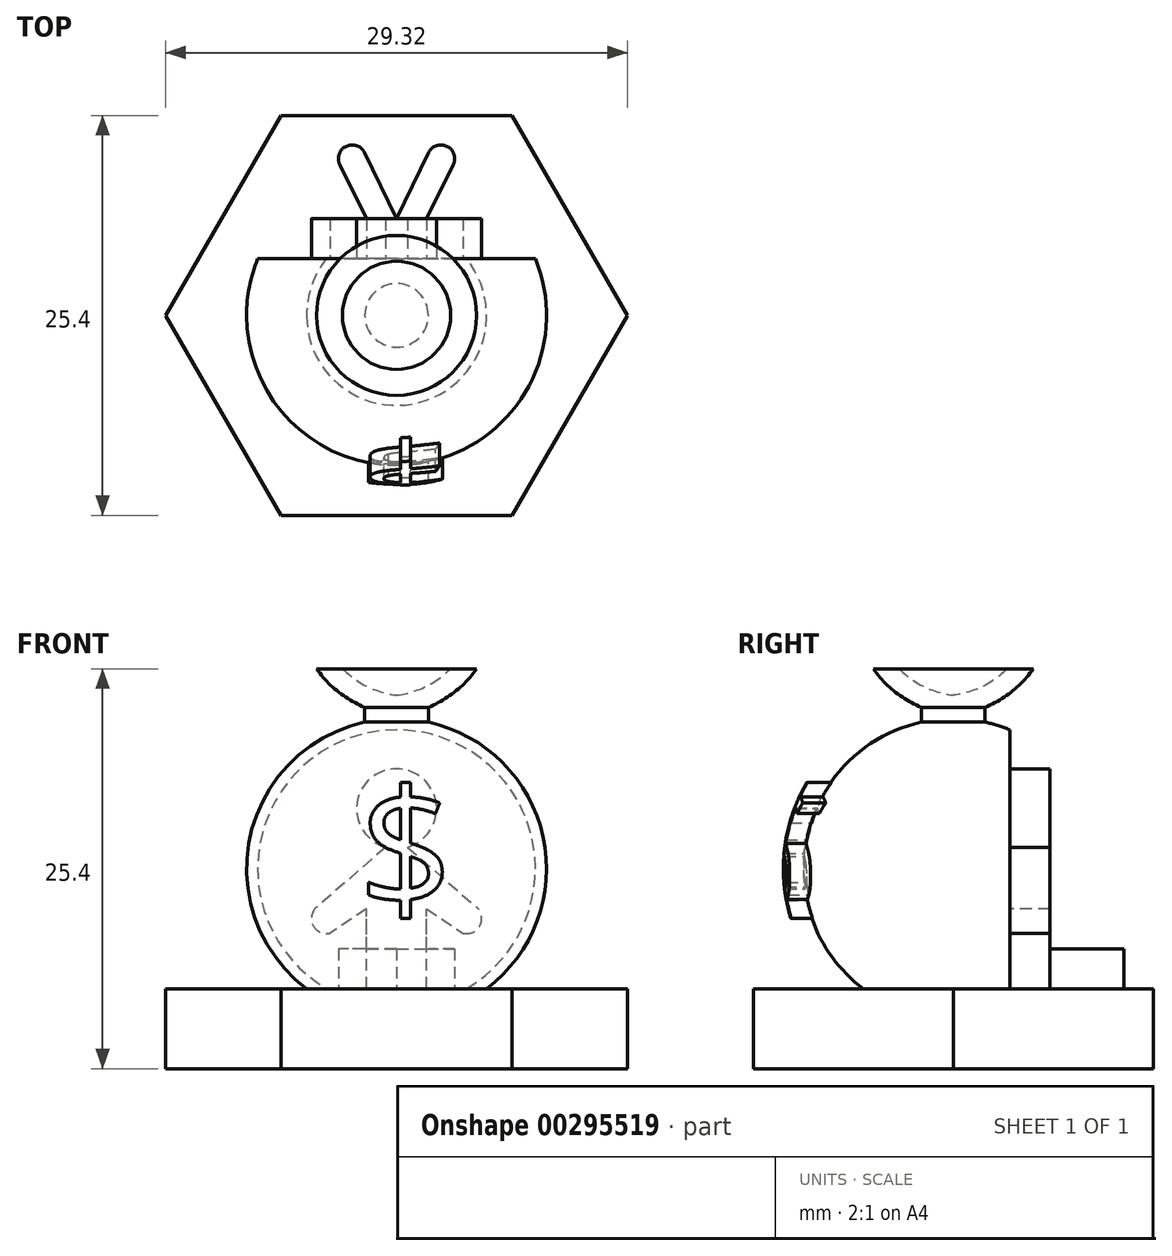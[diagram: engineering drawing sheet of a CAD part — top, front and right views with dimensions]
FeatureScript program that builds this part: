
annotation { "Feature Type Name" : "Feature", "Feature Type Description" : "" }
export const myFeature = defineFeature(function(context is Context, id is Id, definition is map)
    precondition{}
    {
        {
            var Q0;
            Q0=qCreatedBy(makeId("Top.planeOp"),FACE);
            var sketch = newSketch(context, id + "F0", { "sketchPlane" : qUnion([Q0])});
            skCircle(sketch, "E0.cCircle", {"center": v(0, 0) * mm, "radius": 12.7 * mm, "construction": true});
            skLineSegment(sketch, "E0.0", {"start": v(7.33, 12.7) * mm, "end": v(14.66, 0) * mm});
            skLineSegment(sketch, "E0.1", {"start": v(14.66, 0) * mm, "end": v(7.33, -12.7) * mm});
            skLineSegment(sketch, "E0.2", {"start": v(7.33, -12.7) * mm, "end": v(-7.33, -12.7) * mm});
            skLineSegment(sketch, "E0.3", {"start": v(-7.33, -12.7) * mm, "end": v(-14.66, 0) * mm});
            skLineSegment(sketch, "E0.4", {"start": v(-14.66, 0) * mm, "end": v(-7.33, 12.7) * mm});
            skLineSegment(sketch, "E0.5", {"start": v(-7.33, 12.7) * mm, "end": v(7.33, 12.7) * mm});
            skPoint(sketch, "E0.0.midPoint", {"position": v(11, 6.35) * mm});
            skSolve(sketch);
        }
        {
            var Q0;
            Q0 = qSketchRegion(id + "F0", true);
            extrude(context, id + "F1", {"entities" : qUnion([Q0]), "depth" : 5.08 * mm});
        }
        {
            var Q0;
            Q0=qCreatedBy(makeId("Front.planeOp"),FACE);
            var sketch = newSketch(context, id + "F2", { "sketchPlane" : qUnion([Q0])});
            skLineSegment(sketch, "E1", {"start": v(0, 5.08) * mm, "end": v(0, 23.73) * mm});
            skArc(sketch, "E2", {"start": v(-2.02, 22) * mm, "mid": v(-9.3, 14.73) * mm, "end": v(-5.72, 5.08) * mm});
            skLineSegment(sketch, "E3", {"start": v(0, 5.08) * mm, "end": v(-5.72, 5.08) * mm});
            skLineSegment(sketch, "E4", {"start": v(-3.43, 25.4) * mm, "end": v(-5.08, 25.4) * mm});
            skLineSegment(sketch, "E5", {"start": v(-2.02, 22.95) * mm, "end": v(-2.02, 22) * mm});
            skArc(sketch, "E6", {"start": v(-5.08, 25.4) * mm, "mid": v(-3.73, 23.96) * mm, "end": v(-2.02, 22.95) * mm});
            skArc(sketch, "E7.0", {"start": v(-3.43, 25.4) * mm, "mid": v(-1.86, 24.27) * mm, "end": v(0, 23.73) * mm});
            skSolve(sketch);
        }
        {
            var Q0;
            Q0 = qSketchRegion(id + "F2", true);
            var Q1;
            Q1=sQuery(id+"F2.wireOp",EDGE,"E1");
            revolve(context, id + "F3", {"operationType" : NewBodyOperationType.ADD, "entities" : qUnion([Q0]), "axis" : qUnion([Q1]), "revolveType" : RevolveType.FULL});
        }
        {
            var Q0;
            Q0=qCreatedBy(makeId("Front.planeOp"),FACE);
            var sketch = newSketch(context, id + "F4", { "sketchPlane" : qUnion([Q0])});
            skText(sketch, "E8", { "text": "$\n", "fontName": "OpenSans-Regular.ttf"});
            const initialGuessF4  = {"E8": [-0.00245, 0.01016, 1, 0, 0.00762]};
            skSetInitialGuess(sketch, initialGuessF4);
            skSolve(sketch);
        }
        {
            var Q0;
            Q0 = qSketchRegion(id + "F4", true);
            extrude(context, id + "F5", {"entities" : qUnion([Q0]), "operationType" : NewBodyOperationType.ADD, "depth" : 25.4 * mm});
        }
        {
            var Q0;
            Q0=qCreatedBy(makeId("Front.planeOp"),FACE);
            var sketch = newSketch(context, id + "F6", { "sketchPlane" : qUnion([Q0])});
            skLineSegment(sketch, "E9", {"start": v(-63.1, 19.79) * mm, "end": v(-8.14, 19.79) * mm});
            skArc(sketch, "E10.trimOffspring", {"start": v(-8.14, 19.79) * mm, "mid": v(-10.79, 12.34) * mm, "end": v(-7.65, 5.08) * mm});
            skArc(sketch, "E11.trimOffspring", {"start": v(-63.1, 19.79) * mm, "mid": v(-63.5, 12.43) * mm, "end": v(-63.04, 5.08) * mm});
            skLineSegment(sketch, "E12", {"start": v(-7.65, 5.08) * mm, "end": v(-63.04, 5.08) * mm});
            skLineSegment(sketch, "E13", {"start": v(0, 0) * mm, "end": v(0, 12.7) * mm, "construction": true});
            skSolve(sketch);
        }
        {
            var Q0;
            Q0 = qSketchRegion(id + "F6", true);
            var Q1;
            Q1=sQuery(id+"F6.wireOp",EDGE,"E13");
            revolve(context, id + "F7", {"operationType" : NewBodyOperationType.REMOVE, "entities" : qUnion([Q0]), "axis" : qUnion([Q1]), "revolveType" : RevolveType.FULL, "oppositeDirection" : true});
        }
        {
            var Q0;
            Q0=qCreatedBy(makeId("Right.planeOp"),FACE);
            var sketch = newSketch(context, id + "F8", { "sketchPlane" : qUnion([Q0])});
            skLineSegment(sketch, "E14.bottom", {"start": v(3.6, 22.86) * mm, "end": v(22.6, 22.86) * mm});
            skLineSegment(sketch, "E14.top", {"start": v(3.6, 5.08) * mm, "end": v(22.6, 5.08) * mm});
            skLineSegment(sketch, "E14.left", {"start": v(3.6, 22.86) * mm, "end": v(3.6, 5.08) * mm});
            skLineSegment(sketch, "E14.right", {"start": v(22.6, 22.86) * mm, "end": v(22.6, 5.08) * mm});
            skSolve(sketch);
        }
        {
            var Q0;
            Q0 = qSketchRegion(id + "F8", true);
            extrude(context, id + "F9", {"entities" : qUnion([Q0]), "operationType" : NewBodyOperationType.REMOVE, "endBound" : BoundingType.SYMMETRIC, "oppositeDirection" : true, "depth" : 25.4 * mm});
        }
        {
            var Q0;
            Q0=makeQuery(id+"F9.boolean.opBoolean","COPY",FACE,{"derivedFrom":makeQuery(id+"F9.opExtrude","SWEPT_FACE",FACE,{"disambiguationData":[OSD([sQuery(id+"F8.wireOp",EDGE,"E14.left")])]})});
            var sketch = newSketch(context, id + "F10", { "sketchPlane" : qUnion([Q0])});
            skArc(sketch, "E15", {"start": v(0.7, 14.07) * mm, "mid": v(0, 19.05) * mm, "end": v(-0.7, 14.07) * mm});
            skLineSegment(sketch, "E16", {"start": v(0, 16.51) * mm, "end": v(0, 0) * mm, "construction": true});
            skLineSegment(sketch, "E17", {"start": v(0.7, 14.07) * mm, "end": v(5.08, 10.26) * mm});
            skLineSegment(sketch, "E18", {"start": v(1.9, 5.08) * mm, "end": v(1.9, 10.16) * mm});
            skLineSegment(sketch, "E19", {"start": v(1.9, 10.16) * mm, "end": v(4.23, 8.6) * mm});
            skArc(sketch, "E20", {"start": v(4.23, 8.6) * mm, "mid": v(5.3, 9.1) * mm, "end": v(5.08, 10.26) * mm});
            skLineSegment(sketch, "E21.MirrorCS", {"start": v(-0.7, 14.07) * mm, "end": v(-5.08, 10.26) * mm});
            skArc(sketch, "E22.MirrorCS", {"start": v(-4.23, 8.6) * mm, "mid": v(-5.3, 9.1) * mm, "end": v(-5.08, 10.26) * mm});
            skLineSegment(sketch, "E23.MirrorCS", {"start": v(-1.9, 10.16) * mm, "end": v(-4.23, 8.6) * mm});
            skLineSegment(sketch, "E24.MirrorCS", {"start": v(-1.9, 5.08) * mm, "end": v(-1.9, 10.16) * mm});
            skLineSegment(sketch, "E25", {"start": v(-1.9, 5.08) * mm, "end": v(1.9, 5.08) * mm});
            skSolve(sketch);
        }
        {
            var Q0;
            Q0 = qSketchRegion(id + "F10", true);
            extrude(context, id + "F11", {"entities" : qUnion([Q0]), "operationType" : NewBodyOperationType.ADD, "depth" : 2.54 * mm});
        }
        {
            var Q0;
            Q0=makeQuery(id+"F9.boolean.opBoolean","MERGE",FACE,{"derivedFrom":[makeQuery(id+"F1.opExtrude","CAP_FACE",FACE,{"disambiguationData":[OSD([sQuery(id+"F0.wireOp",EDGE,"E0.0"),sQuery(id+"F0.wireOp",EDGE,"E0.1"),sQuery(id+"F0.wireOp",EDGE,"E0.2"),sQuery(id+"F0.wireOp",EDGE,"E0.3"),sQuery(id+"F0.wireOp",EDGE,"E0.4"),sQuery(id+"F0.wireOp",EDGE,"E0.5")])],"isStart":false}),makeQuery(id+"F9.opExtrude","SWEPT_FACE",FACE,{"disambiguationData":[OSD([sQuery(id+"F8.wireOp",EDGE,"E14.top")])]})]});
            var sketch = newSketch(context, id + "F12", { "sketchPlane" : qUnion([Q0])});
            skLineSegment(sketch, "E26", {"start": v(-1.9, 6.14) * mm, "end": v(-3.6, 9.55) * mm});
            skLineSegment(sketch, "E27", {"start": v(0, 6.14) * mm, "end": v(-2.03, 10.33) * mm});
            skArc(sketch, "E28", {"start": v(-2.03, 10.33) * mm, "mid": v(-3.2, 10.73) * mm, "end": v(-3.6, 9.55) * mm});
            skLineSegment(sketch, "E29", {"start": v(0, 6.14) * mm, "end": v(0, 11.32) * mm, "construction": true});
            skLineSegment(sketch, "E30.MirrorCS", {"start": v(0, 6.14) * mm, "end": v(2.03, 10.33) * mm});
            skArc(sketch, "E31.MirrorCS", {"start": v(2.03, 10.33) * mm, "mid": v(3.2, 10.73) * mm, "end": v(3.6, 9.55) * mm});
            skLineSegment(sketch, "E32.MirrorCS", {"start": v(1.9, 6.14) * mm, "end": v(3.6, 9.55) * mm});
            skLineSegment(sketch, "E33", {"start": v(-1.9, 6.14) * mm, "end": v(1.9, 6.14) * mm});
            skSolve(sketch);
        }
        {
            var Q0;
            {var subQ0=sQuery(id+"F12.wireOp",EDGE,"E30.MirrorCS");Q0=makeQuery(id+"F12.imprint","IMPRINT",FACE,{"disambiguationData":[TD([[makeQuery(id+"F12.imprint","IMPRINT",EDGE,{"derivedFrom":subQ0}),-1.0]])]});}
            var Q1;
            {var subQ0=sQuery(id+"F12.wireOp",EDGE,"E26");Q1=makeQuery(id+"F12.imprint","IMPRINT",FACE,{"disambiguationData":[TD([[makeQuery(id+"F12.imprint","IMPRINT",EDGE,{"derivedFrom":subQ0}),-1.0]])]});}
            var Q2;
            Q2 = qConstructionFilter(qBodyType(qCreatedBy(id + "F12" ,EDGE), BodyType.WIRE), ConstructionObject.NO);
            extrude(context, id + "F13", {"entities" : qUnion([Q0, Q1]), "operationType" : NewBodyOperationType.ADD, "surfaceEntities" : qUnion([Q2]), "depth" : 2.54 * mm});
        }
    });
